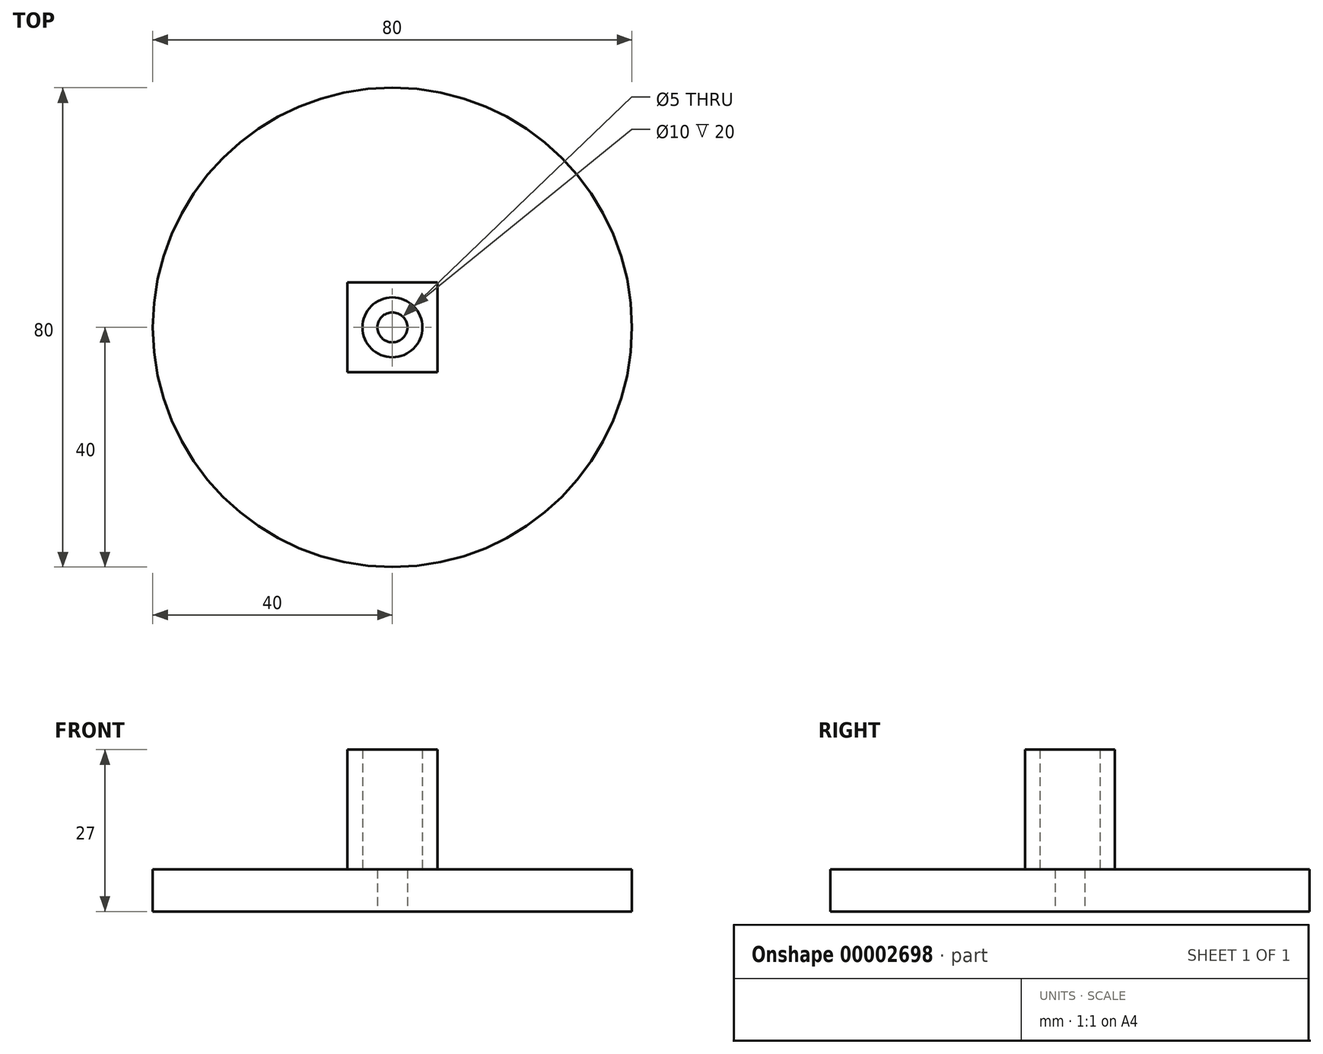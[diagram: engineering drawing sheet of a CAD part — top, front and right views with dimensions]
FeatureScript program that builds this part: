
annotation { "Feature Type Name" : "Feature", "Feature Type Description" : "" }
export const myFeature = defineFeature(function(context is Context, id is Id, definition is map)
    precondition{}
    {
        {
            var Q0;
            Q0=qCreatedBy(makeId("Top.planeOp"),FACE);
            var sketch = newSketch(context, id + "F0", { "sketchPlane" : qUnion([Q0])});
            skCircle(sketch, "E0", {"center": v(0, 0) * mm, "radius": 40 * mm});
            skLineSegment(sketch, "E1.bottom", {"start": v(-7.5, 7.5) * mm, "end": v(7.5, 7.5) * mm});
            skLineSegment(sketch, "E1.top", {"start": v(-7.5, -7.5) * mm, "end": v(7.5, -7.5) * mm});
            skLineSegment(sketch, "E1.left", {"start": v(-7.5, 7.5) * mm, "end": v(-7.5, -7.5) * mm});
            skLineSegment(sketch, "E1.right", {"start": v(7.5, 7.5) * mm, "end": v(7.5, -7.5) * mm});
            skPoint(sketch, "E2", {"position": v(0, 7.5) * mm});
            skPoint(sketch, "E3", {"position": v(7.5, 0) * mm});
            skCircle(sketch, "E4", {"center": v(0, 0) * mm, "radius": 5 * mm});
            skCircle(sketch, "E5", {"center": v(0, 0) * mm, "radius": 2.5 * mm});
            skSolve(sketch);
        }
        {
            var Q0;
            Q0 = qSketchRegion(id + "F0", true);
            var Q1;
            Q1=makeQuery(id+"F0.imprint","IMPRINT",FACE,{"disambiguationData":[TD([[makeQuery(id+"F0.imprint","IMPRINT",EDGE,{"derivedFrom":sQuery(id+"F0.wireOp",EDGE,"E1.bottom")}),-1.0]])]});
            var Q2;
            Q2=makeQuery(id+"F0.imprint","IMPRINT",FACE,{"disambiguationData":[TD([[makeQuery(id+"F0.imprint","IMPRINT",EDGE,{"derivedFrom":sQuery(id+"F0.wireOp",EDGE,"E4")}),1.0]])]});
            extrude(context, id + "F1", {"entities" : qUnion([Q0, Q1, Q2]), "depth" : 7 * mm});
        }
        {
            var Q0;
            Q0=makeQuery(id+"F0.imprint","IMPRINT",FACE,{"disambiguationData":[TD([[makeQuery(id+"F0.imprint","IMPRINT",EDGE,{"derivedFrom":sQuery(id+"F0.wireOp",EDGE,"E1.bottom")}),-1.0]])]});
            extrude(context, id + "F2", {"entities" : qUnion([Q0]), "operationType" : NewBodyOperationType.ADD, "depth" : 27 * mm});
        }
    });
